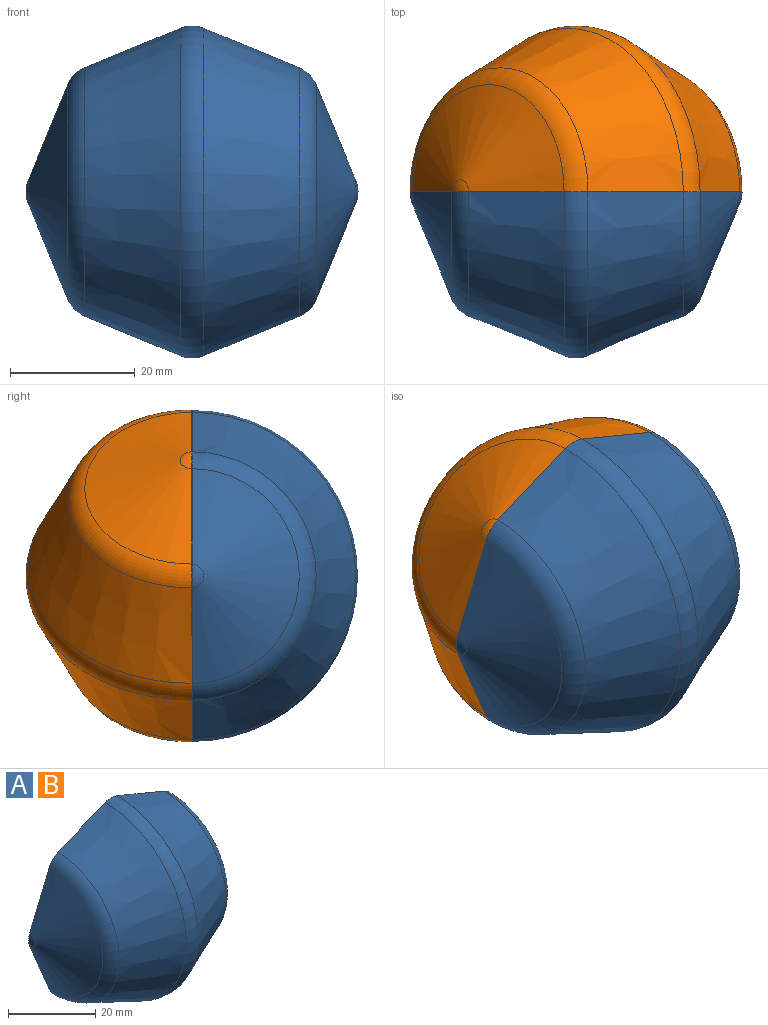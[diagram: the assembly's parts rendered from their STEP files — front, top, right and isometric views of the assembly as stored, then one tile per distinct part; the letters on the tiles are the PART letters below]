
ASSEMBLY  parts=2 mates=1
PART A: 10 faces, bbox 53.3x28.8x57.7 mm
  f0: sphere r=5mm, area 6mm2, adj f1,f9
  f1: cone r=1.91mm half-angle=67.5deg, axis (-1,0,0), area 498mm2, adj f0,f2,f9
  f2: torus R=15.31mm, axis (-1,0,0), area 231.4mm2, adj f1,f3,f9
  f3: cone r=19.93mm half-angle=22.5deg, axis (-1,0,0), area 1202.2mm2, adj f2,f4,f9
  f4: torus R=21.65mm, axis (-1,0,0), area 327.2mm2, adj f3,f5,f9
  f5: cone r=26.27mm half-angle=22.5deg, axis (1,0,0), area 1202.2mm2, adj f4,f6,f9
  f6: torus R=15.31mm, axis (-1,0,0), area 231.4mm2, adj f5,f7,f9
  f7: cone r=17.22mm half-angle=67.5deg, axis (1,0,0), area 498mm2, adj f6,f8,f9
  f8: sphere r=5mm, area 6mm2, adj f7,f9
  f9: plane 53.3x53.3mm, normal (0,1,0), area 2066.8mm2, adj f0,f1,f2,f3,f4,f5,f6,f7
PART B: same geometry as A
PLACE A at identity fixed
PLACE B rot(axis=(0.92,0,-0.38),180deg) t=(0,0,0)mm
MATE parallel B.f9 <-> A.f9  axis (0,-1,0) through (0,0,0)mm
